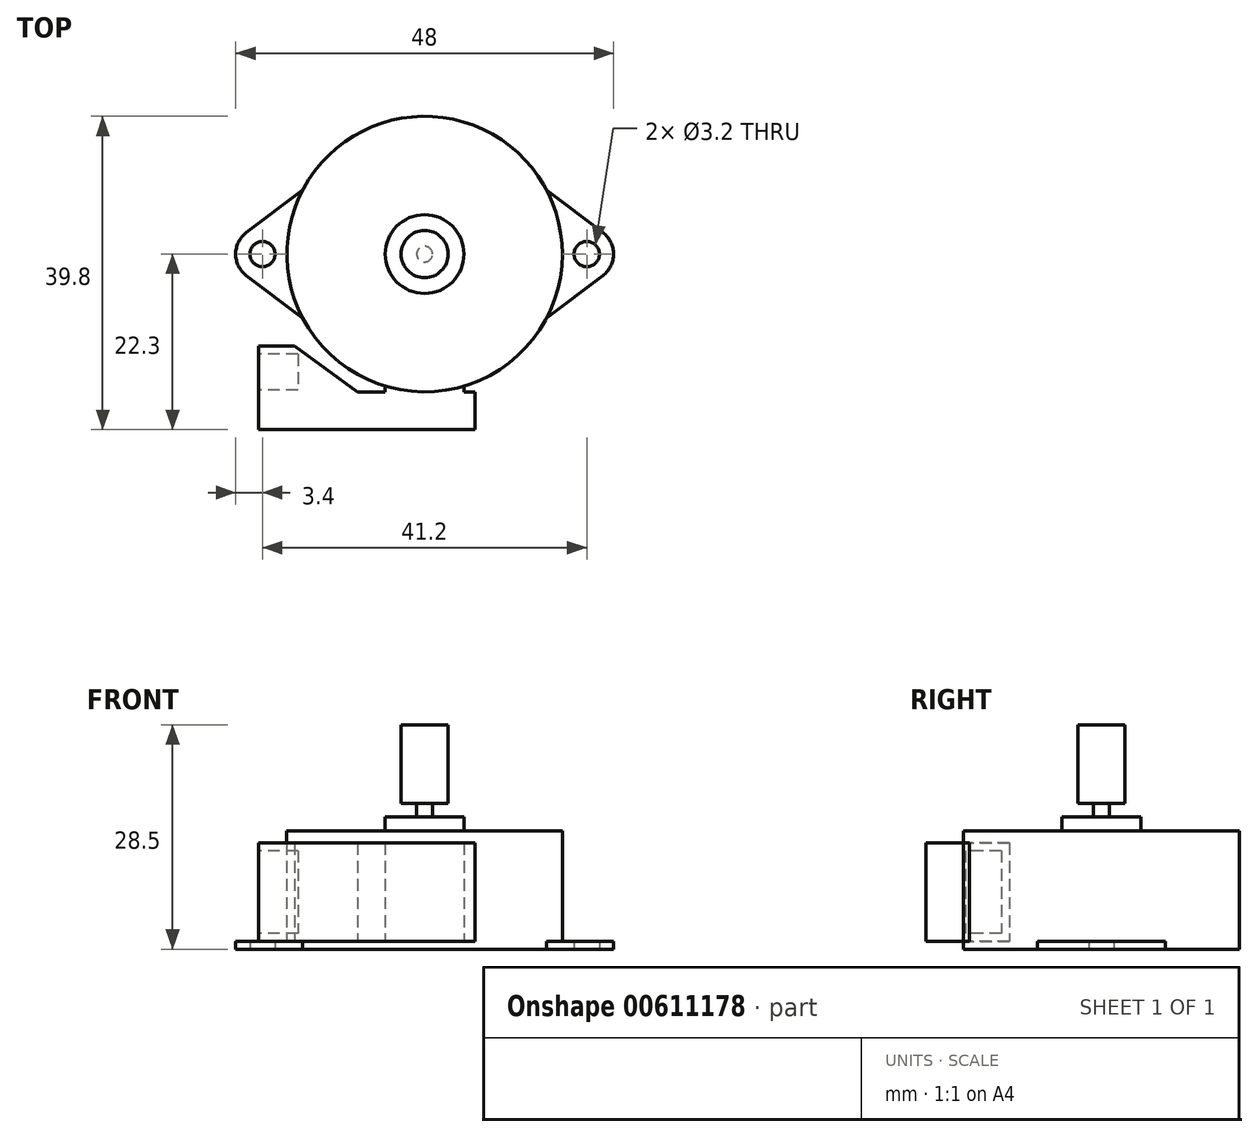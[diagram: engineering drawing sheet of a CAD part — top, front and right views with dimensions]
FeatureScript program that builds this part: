
annotation { "Feature Type Name" : "Feature", "Feature Type Description" : "" }
export const myFeature = defineFeature(function(context is Context, id is Id, definition is map)
    precondition{}
    {
        {
            var Q0;
            Q0=qCreatedBy(makeId("Top.planeOp"),FACE);
            var sketch = newSketch(context, id + "F0", { "sketchPlane" : qUnion([Q0])});
            skCircle(sketch, "E0", {"center": v(0, 0) * mm, "radius": 17.5 * mm});
            skCircle(sketch, "E1", {"center": v(-20.6, 0) * mm, "radius": 1.6 * mm});
            skCircle(sketch, "E2", {"center": v(-20.6, 0) * mm, "radius": 3.4 * mm});
            skLineSegment(sketch, "E3", {"start": v(-22.65, 2.71) * mm, "end": v(-15.5, 8.12) * mm});
            skLineSegment(sketch, "E4", {"start": v(-15.5, 8.12) * mm, "end": v(-15.5, -8.12) * mm});
            skLineSegment(sketch, "E5", {"start": v(-15.5, -8.12) * mm, "end": v(-22.65, -2.71) * mm});
            skLineSegment(sketch, "E6", {"start": v(-22.65, -2.71) * mm, "end": v(-22.65, 2.71) * mm});
            skLineSegment(sketch, "E7.MirrorCS", {"start": v(15.5, 8.12) * mm, "end": v(15.5, -8.12) * mm});
            skLineSegment(sketch, "E8.MirrorCS", {"start": v(15.5, -8.12) * mm, "end": v(22.65, -2.71) * mm});
            skLineSegment(sketch, "E9.MirrorCS", {"start": v(22.65, 2.71) * mm, "end": v(15.5, 8.12) * mm});
            skCircle(sketch, "E10.MirrorC", {"center": v(20.6, 0) * mm, "radius": 3.4 * mm});
            skCircle(sketch, "E11.MirrorC", {"center": v(20.6, 0) * mm, "radius": 1.6 * mm});
            skLineSegment(sketch, "E12.MirrorCS", {"start": v(22.65, -2.71) * mm, "end": v(22.65, 2.71) * mm});
            skSolve(sketch);
        }
        {
            var Q0;
            Q0=qSketchRegion(id+"F0",true);
            var Q1;
            {var subQ0=sQuery(id+"F0.wireOp",EDGE,"E2");var subQ1=sQuery(id+"F0.wireOp",EDGE,"E0");var subQ2=makeQuery(id+"F0.imprint","INTERSECT",VERTEX,{"disambiguationData":[OD(0.0)],"derivedFrom":[subQ1,subQ0]});Q1=makeQuery(id+"F0.imprint","IMPRINT",FACE,{"disambiguationData":[TD([[makeQuery(id+"F0.imprint","IMPRINT",EDGE,{"disambiguationData":[TD([[subQ2,-1.0]])],"derivedFrom":subQ1}),1.0]])]});}
            var Q2;
            {var subQ0=sQuery(id+"F0.wireOp",EDGE,"E10.MirrorC");var subQ1=sQuery(id+"F0.wireOp",EDGE,"E0");var subQ2=makeQuery(id+"F0.imprint","INTERSECT",VERTEX,{"disambiguationData":[OD(0.0)],"derivedFrom":[subQ1,subQ0]});Q2=makeQuery(id+"F0.imprint","IMPRINT",FACE,{"disambiguationData":[TD([[makeQuery(id+"F0.imprint","IMPRINT",EDGE,{"disambiguationData":[TD([[subQ2,1.0]])],"derivedFrom":subQ1}),1.0]])]});}
            extrude(context, id + "F1", {"entities" : qUnion([Q0, Q1, Q2]), "depth" : 1 * mm, "offsetDistance" : 25.4 * mm});
        }
        {
            var Q0;
            Q0=makeQuery(id+"F1.opExtrude","CAP_FACE",FACE,{"disambiguationData":[OSD([sQuery(id+"F0.wireOp",EDGE,"E0"),sQuery(id+"F0.wireOp",EDGE,"E1"),sQuery(id+"F0.wireOp",EDGE,"E2"),sQuery(id+"F0.wireOp",EDGE,"E3"),sQuery(id+"F0.wireOp",EDGE,"E5"),sQuery(id+"F0.wireOp",EDGE,"E8.MirrorCS"),sQuery(id+"F0.wireOp",EDGE,"E9.MirrorCS"),sQuery(id+"F0.wireOp",EDGE,"E10.MirrorC"),sQuery(id+"F0.wireOp",EDGE,"E11.MirrorC")])],"isStart":false});
            var sketch = newSketch(context, id + "F2", { "sketchPlane" : qUnion([Q0])});
            skCircle(sketch, "E13", {"center": v(0, 0) * mm, "radius": 17.5 * mm});
            skLineSegment(sketch, "E14.bottom", {"start": v(-21.1, -17.5) * mm, "end": v(6.4, -17.5) * mm});
            skLineSegment(sketch, "E14.top", {"start": v(-21.1, -22.3) * mm, "end": v(6.4, -22.3) * mm});
            skLineSegment(sketch, "E14.left", {"start": v(-21.1, -17.5) * mm, "end": v(-21.1, -22.3) * mm});
            skLineSegment(sketch, "E14.right", {"start": v(6.4, -17.5) * mm, "end": v(6.4, -22.3) * mm});
            skLineSegment(sketch, "E15", {"start": v(-21.1, -17.5) * mm, "end": v(-21.1, -11.7) * mm});
            skLineSegment(sketch, "E16", {"start": v(-21.1, -11.7) * mm, "end": v(-16.5, -11.7) * mm});
            skLineSegment(sketch, "E17", {"start": v(-16.5, -11.7) * mm, "end": v(-8.48, -17.5) * mm});
            skLineSegment(sketch, "E18.bottom", {"start": v(-5, 0) * mm, "end": v(5, 0) * mm});
            skLineSegment(sketch, "E18.top", {"start": v(-5, -22.3) * mm, "end": v(5, -22.3) * mm});
            skLineSegment(sketch, "E18.left", {"start": v(-5, 0) * mm, "end": v(-5, -22.3) * mm});
            skLineSegment(sketch, "E18.right", {"start": v(5, 0) * mm, "end": v(5, -22.3) * mm});
            skSolve(sketch);
        }
        {
            var Q0;
            {var subQ5=sQuery(id+"F2.wireOp",EDGE,"E18.bottom");Q0=makeQuery(id+"F2.imprint","IMPRINT",FACE,{"disambiguationData":[TD([[makeQuery(id+"F2.imprint","IMPRINT",EDGE,{"derivedFrom":subQ5}),1.0]])]});}
            var Q1;
            {var subQ1=sQuery(id+"F2.wireOp",EDGE,"E18.bottom");Q1=makeQuery(id+"F2.imprint","IMPRINT",FACE,{"disambiguationData":[TD([[makeQuery(id+"F2.imprint","IMPRINT",EDGE,{"derivedFrom":subQ1}),-1.0]])]});}
            extrude(context, id + "F3", {"entities" : qUnion([Q0, Q1]), "operationType" : NewBodyOperationType.ADD, "depth" : 14 * mm, "offsetDistance" : 25.4 * mm});
        }
        {
            var Q0;
            Q0=qSketchRegion(id+"F2",true);
            extrude(context, id + "F4", {"entities" : qUnion([Q0]), "operationType" : NewBodyOperationType.ADD, "depth" : 12.5 * mm, "offsetDistance" : 25.4 * mm});
        }
        {
            var Q0;
            Q0=makeQuery(id+"F3.opExtrude","CAP_FACE",FACE,{"disambiguationData":[OSD([sQuery(id+"F2.wireOp",EDGE,"E13")])],"isStart":false});
            var sketch = newSketch(context, id + "F5", { "sketchPlane" : qUnion([Q0])});
            skCircle(sketch, "E19", {"center": v(0, 0) * mm, "radius": 5 * mm});
            skSolve(sketch);
        }
        {
            var Q0;
            Q0=qSketchRegion(id+"F5",true);
            extrude(context, id + "F6", {"entities" : qUnion([Q0]), "operationType" : NewBodyOperationType.ADD, "depth" : 1.8 * mm, "offsetDistance" : 25.4 * mm});
        }
        {
            var Q0;
            Q0=makeQuery(id+"F6.opExtrude","CAP_FACE",FACE,{"disambiguationData":[OSD([sQuery(id+"F5.wireOp",EDGE,"E19")])],"isStart":false});
            var sketch = newSketch(context, id + "F7", { "sketchPlane" : qUnion([Q0])});
            skCircle(sketch, "E20", {"center": v(0, 0) * mm, "radius": 1 * mm});
            skSolve(sketch);
        }
        {
            var Q0;
            Q0=qSketchRegion(id+"F7",true);
            extrude(context, id + "F8", {"entities" : qUnion([Q0]), "operationType" : NewBodyOperationType.ADD, "depth" : 1.7 * mm, "offsetDistance" : 25.4 * mm});
        }
        {
            var Q0;
            Q0=makeQuery(id+"F8.opExtrude","CAP_FACE",FACE,{"disambiguationData":[OSD([sQuery(id+"F7.wireOp",EDGE,"E20")])],"isStart":false});
            var sketch = newSketch(context, id + "F9", { "sketchPlane" : qUnion([Q0])});
            skCircle(sketch, "E21", {"center": v(0, 0) * mm, "radius": 3 * mm});
            skSolve(sketch);
        }
        {
            var Q0;
            Q0=qSketchRegion(id+"F9",true);
            extrude(context, id + "F10", {"entities" : qUnion([Q0]), "operationType" : NewBodyOperationType.ADD, "depth" : 10 * mm, "offsetDistance" : 25.4 * mm});
        }
        {
            var Q0;
            Q0=makeQuery(id+"F4.opExtrude","SWEPT_FACE",FACE,{"disambiguationData":[OSD([sQuery(id+"F2.wireOp",EDGE,"E14.left"),sQuery(id+"F2.wireOp",EDGE,"E15")])]});
            var sketch = newSketch(context, id + "F11", { "sketchPlane" : qUnion([Q0])});
            skLineSegment(sketch, "E22.bottom", {"start": v(12.7, 12.5) * mm, "end": v(17.3, 12.5) * mm});
            skLineSegment(sketch, "E22.top", {"start": v(12.7, 2) * mm, "end": v(17.3, 2) * mm});
            skLineSegment(sketch, "E22.left", {"start": v(12.7, 12.5) * mm, "end": v(12.7, 2) * mm});
            skLineSegment(sketch, "E22.right", {"start": v(17.3, 12.5) * mm, "end": v(17.3, 2) * mm});
            skSolve(sketch);
        }
        {
            var Q0;
            Q0=qSketchRegion(id+"F11",true);
            extrude(context, id + "F12", {"entities" : qUnion([Q0]), "operationType" : NewBodyOperationType.REMOVE, "oppositeDirection" : true, "depth" : 5 * mm, "offsetDistance" : 25.4 * mm});
        }
    });
